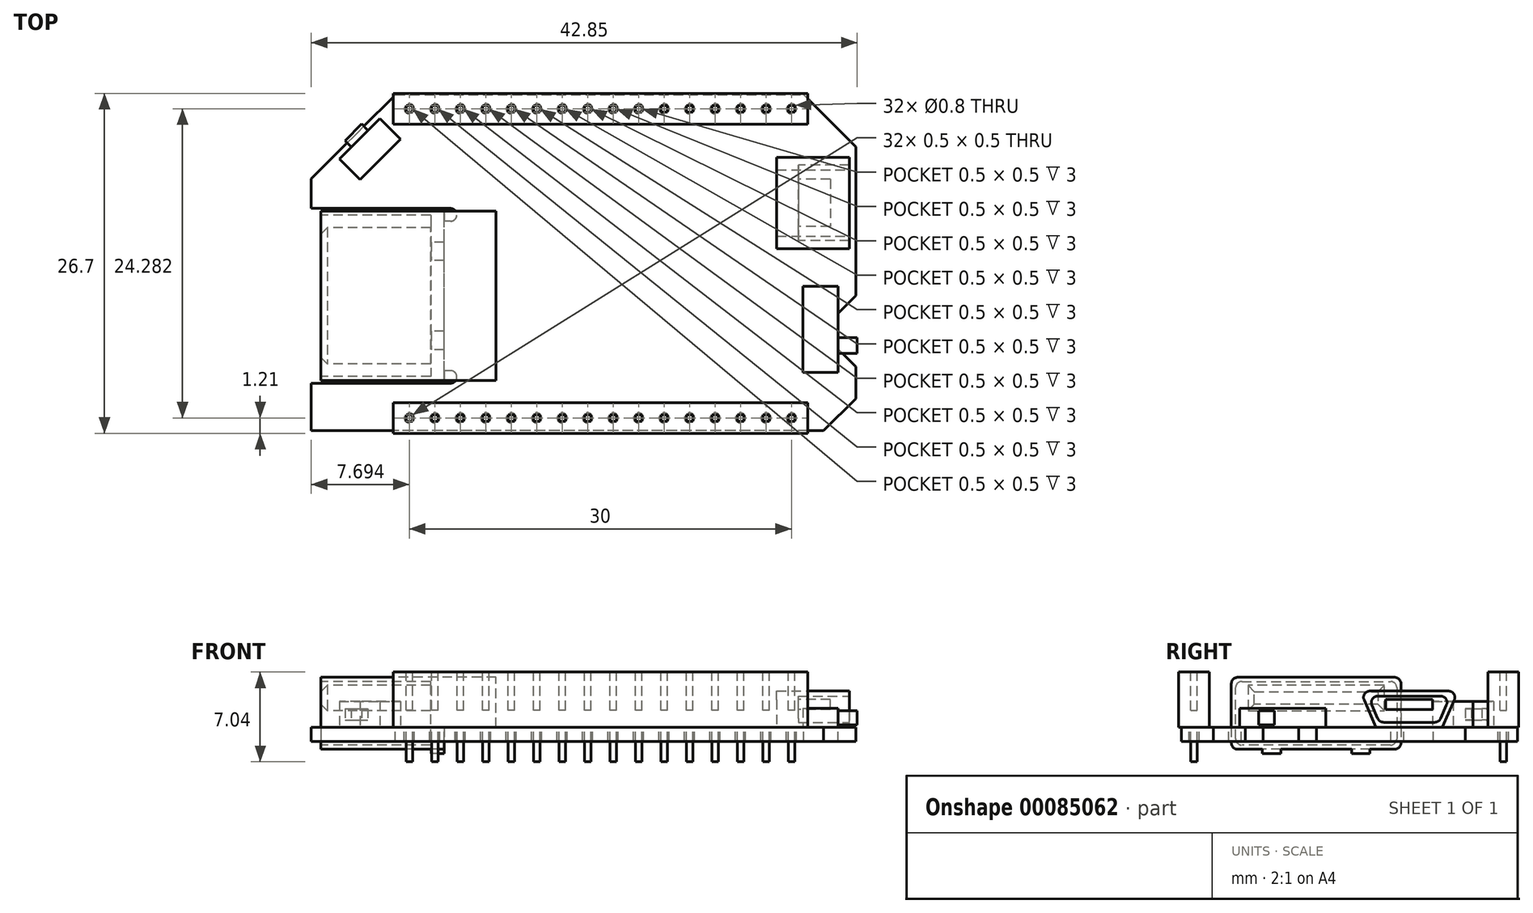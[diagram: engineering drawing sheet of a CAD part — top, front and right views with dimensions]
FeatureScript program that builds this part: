
annotation { "Feature Type Name" : "Feature", "Feature Type Description" : "" }
export const myFeature = defineFeature(function(context is Context, id is Id, definition is map)
    precondition{}
    {
        {
            var Q0;
            Q0=qCreatedBy(makeId("Top.planeOp"),FACE);
            var sketch = newSketch(context, id + "F0", { "sketchPlane" : qUnion([Q0])});
            skLineSegment(sketch, "E0", {"start": v(0, 19.78) * mm, "end": v(6.6, 26.37) * mm});
            skLineSegment(sketch, "E1", {"start": v(6.6, 26.37) * mm, "end": v(38.67, 26.37) * mm});
            skLineSegment(sketch, "E2", {"start": v(38.67, 26.37) * mm, "end": v(42.74, 22.3) * mm});
            skLineSegment(sketch, "E3", {"start": v(42.74, 22.3) * mm, "end": v(42.74, 10.6) * mm});
            skLineSegment(sketch, "E4", {"start": v(42.74, 2.52) * mm, "end": v(40.22, 0) * mm});
            skPoint(sketch, "E5.end.orphan", {"position": v(0, 0) * mm});
            skLineSegment(sketch, "E6", {"start": v(40.22, 0) * mm, "end": v(0, 0) * mm});
            skLineSegment(sketch, "E7", {"start": v(0, 3.71) * mm, "end": v(10.43, 3.71) * mm});
            skLineSegment(sketch, "E8", {"start": v(10.43, 3.71) * mm, "end": v(10.43, 17.45) * mm});
            skLineSegment(sketch, "E9", {"start": v(10.43, 17.45) * mm, "end": v(0, 17.45) * mm});
            skLineSegment(sketch, "E10", {"start": v(0, 17.45) * mm, "end": v(0, 19.78) * mm});
            skLineSegment(sketch, "E11", {"start": v(0, 3.71) * mm, "end": v(0, 0) * mm});
            skLineSegment(sketch, "E12", {"start": v(42.74, 10.6) * mm, "end": v(41.35, 9.2) * mm});
            skLineSegment(sketch, "E13", {"start": v(41.35, 9.2) * mm, "end": v(41.35, 6.41) * mm});
            skLineSegment(sketch, "E14", {"start": v(41.35, 6.41) * mm, "end": v(42.74, 5.02) * mm});
            skLineSegment(sketch, "E15.trimOffspring", {"start": v(42.74, 5.02) * mm, "end": v(42.74, 2.52) * mm});
            skSolve(sketch);
        }
        {
            var Q0;
            Q0 = qSketchRegion(id + "F0", true);
            extrude(context, id + "F1", {"entities" : qUnion([Q0]), "oppositeDirection" : true, "depth" : 1.1 * mm});
        }
        {
            var Q0;
            Q0=makeQuery(id+"F1.opExtrude","CAP_FACE",FACE,{"disambiguationData":[OSD([sQuery(id+"F0.wireOp",EDGE,"E0"),sQuery(id+"F0.wireOp",EDGE,"E1"),sQuery(id+"F0.wireOp",EDGE,"E2"),sQuery(id+"F0.wireOp",EDGE,"E3"),sQuery(id+"F0.wireOp",EDGE,"E4"),sQuery(id+"F0.wireOp",EDGE,"E6"),sQuery(id+"F0.wireOp",EDGE,"E7"),sQuery(id+"F0.wireOp",EDGE,"E8"),sQuery(id+"F0.wireOp",EDGE,"E9"),sQuery(id+"F0.wireOp",EDGE,"E10"),sQuery(id+"F0.wireOp",EDGE,"E11")])],"isStart":true});
            var sketch = newSketch(context, id + "F2", { "sketchPlane" : qUnion([Q0])});
            skArc(sketch, "E16", {"start": v(10.93, 16.45) * mm, "mid": v(11.43, 16.95) * mm, "end": v(10.93, 17.45) * mm});
            skArc(sketch, "E17", {"start": v(10.93, 3.71) * mm, "mid": v(11.43, 4.21) * mm, "end": v(10.93, 4.71) * mm});
            skLineSegment(sketch, "E18", {"start": v(10.43, 17.45) * mm, "end": v(10.93, 17.45) * mm});
            skLineSegment(sketch, "E19", {"start": v(10.93, 16.45) * mm, "end": v(10.43, 16.45) * mm});
            skLineSegment(sketch, "E20", {"start": v(10.43, 17.45) * mm, "end": v(10.43, 16.45) * mm});
            skPoint(sketch, "E21", {"position": v(11.43, 16.95) * mm});
            skLineSegment(sketch, "E22", {"start": v(10.43, 3.71) * mm, "end": v(10.93, 3.71) * mm});
            skLineSegment(sketch, "E23", {"start": v(10.43, 3.71) * mm, "end": v(10.43, 4.71) * mm});
            skLineSegment(sketch, "E24", {"start": v(10.43, 4.71) * mm, "end": v(10.93, 4.71) * mm});
            skSolve(sketch);
        }
        {
            var Q0;
            Q0 = qSketchRegion(id + "F2", true);
            extrude(context, id + "F3", {"entities" : qUnion([Q0]), "operationType" : NewBodyOperationType.REMOVE, "endBound" : BoundingType.THROUGH_ALL, "oppositeDirection" : true, "depth" : 25 * mm});
        }
        {
            var Q0;
            Q0=makeQuery(id+"F1.opExtrude","CAP_FACE",FACE,{"disambiguationData":[OSD([sQuery(id+"F0.wireOp",EDGE,"E0"),sQuery(id+"F0.wireOp",EDGE,"E1"),sQuery(id+"F0.wireOp",EDGE,"E2"),sQuery(id+"F0.wireOp",EDGE,"E3"),sQuery(id+"F0.wireOp",EDGE,"E4"),sQuery(id+"F0.wireOp",EDGE,"E6"),sQuery(id+"F0.wireOp",EDGE,"E7"),sQuery(id+"F0.wireOp",EDGE,"E8"),sQuery(id+"F0.wireOp",EDGE,"E9"),sQuery(id+"F0.wireOp",EDGE,"E10"),sQuery(id+"F0.wireOp",EDGE,"E11")])],"isStart":true});
            var sketch = newSketch(context, id + "F4", { "sketchPlane" : qUnion([Q0])});
            skCircle(sketch, "E25", {"center": v(7.7, 1) * mm, "radius": 0.4 * mm});
            skCircle(sketch, "E26", {"center": v(7.7, 25.27) * mm, "radius": 0.4 * mm});
            skCircle(sketch, "E27.1.0.0", {"center": v(9.7, 0.99) * mm, "radius": 0.4 * mm});
            skCircle(sketch, "E27.1.0.1", {"center": v(9.7, 25.27) * mm, "radius": 0.4 * mm});
            skCircle(sketch, "E27.2.0.0", {"center": v(11.7, 0.99) * mm, "radius": 0.4 * mm});
            skCircle(sketch, "E27.2.0.1", {"center": v(11.7, 25.27) * mm, "radius": 0.4 * mm});
            skLineSegment(sketch, "E27.direction1", {"start": v(7.7, 1) * mm, "end": v(9.7, 1) * mm, "construction": true});
            skCircle(sketch, "E28.0.3.0", {"center": v(13.7, 0.99) * mm, "radius": 0.4 * mm});
            skCircle(sketch, "E28.2.3.0", {"center": v(13.7, 25.27) * mm, "radius": 0.4 * mm});
            skCircle(sketch, "E28.0.4.0", {"center": v(15.7, 0.99) * mm, "radius": 0.4 * mm});
            skCircle(sketch, "E28.2.4.0", {"center": v(15.7, 25.27) * mm, "radius": 0.4 * mm});
            skCircle(sketch, "E28.0.5.0", {"center": v(17.7, 0.99) * mm, "radius": 0.4 * mm});
            skCircle(sketch, "E28.2.5.0", {"center": v(17.7, 25.27) * mm, "radius": 0.4 * mm});
            skCircle(sketch, "E28.0.6.0", {"center": v(19.7, 0.99) * mm, "radius": 0.4 * mm});
            skCircle(sketch, "E28.2.6.0", {"center": v(19.7, 25.27) * mm, "radius": 0.4 * mm});
            skCircle(sketch, "E28.0.7.0", {"center": v(21.7, 0.99) * mm, "radius": 0.4 * mm});
            skCircle(sketch, "E28.2.7.0", {"center": v(21.7, 25.27) * mm, "radius": 0.4 * mm});
            skCircle(sketch, "E28.0.8.0", {"center": v(23.7, 0.99) * mm, "radius": 0.4 * mm});
            skCircle(sketch, "E28.2.8.0", {"center": v(23.7, 25.27) * mm, "radius": 0.4 * mm});
            skCircle(sketch, "E28.0.9.0", {"center": v(25.7, 0.99) * mm, "radius": 0.4 * mm});
            skCircle(sketch, "E28.2.9.0", {"center": v(25.7, 25.27) * mm, "radius": 0.4 * mm});
            skCircle(sketch, "E28.0.10.0", {"center": v(27.7, 0.99) * mm, "radius": 0.4 * mm});
            skCircle(sketch, "E28.2.10.0", {"center": v(27.7, 25.27) * mm, "radius": 0.4 * mm});
            skCircle(sketch, "E28.0.11.0", {"center": v(29.7, 0.99) * mm, "radius": 0.4 * mm});
            skCircle(sketch, "E28.2.11.0", {"center": v(29.7, 25.27) * mm, "radius": 0.4 * mm});
            skCircle(sketch, "E28.0.12.0", {"center": v(31.7, 0.99) * mm, "radius": 0.4 * mm});
            skCircle(sketch, "E28.2.12.0", {"center": v(31.7, 25.27) * mm, "radius": 0.4 * mm});
            skCircle(sketch, "E28.0.13.0", {"center": v(33.7, 0.99) * mm, "radius": 0.4 * mm});
            skCircle(sketch, "E28.2.13.0", {"center": v(33.7, 25.27) * mm, "radius": 0.4 * mm});
            skCircle(sketch, "E28.0.14.0", {"center": v(35.7, 0.99) * mm, "radius": 0.4 * mm});
            skCircle(sketch, "E28.2.14.0", {"center": v(35.7, 25.27) * mm, "radius": 0.4 * mm});
            skCircle(sketch, "E28.0.15.0", {"center": v(37.7, 0.99) * mm, "radius": 0.4 * mm});
            skCircle(sketch, "E28.2.15.0", {"center": v(37.7, 25.27) * mm, "radius": 0.4 * mm});
            skSolve(sketch);
        }
        {
            var Q0;
            Q0 = qSketchRegion(id + "F4", true);
            extrude(context, id + "F5", {"entities" : qUnion([Q0]), "operationType" : NewBodyOperationType.REMOVE, "endBound" : BoundingType.THROUGH_ALL, "oppositeDirection" : true, "depth" : 25 * mm});
        }
        {
            var Q0;
            Q0=makeQuery(id+"F1.opExtrude","CAP_FACE",FACE,{"disambiguationData":[OSD([sQuery(id+"F0.wireOp",EDGE,"E0"),sQuery(id+"F0.wireOp",EDGE,"E1"),sQuery(id+"F0.wireOp",EDGE,"E2"),sQuery(id+"F0.wireOp",EDGE,"E3"),sQuery(id+"F0.wireOp",EDGE,"E4"),sQuery(id+"F0.wireOp",EDGE,"E6"),sQuery(id+"F0.wireOp",EDGE,"E7"),sQuery(id+"F0.wireOp",EDGE,"E8"),sQuery(id+"F0.wireOp",EDGE,"E9"),sQuery(id+"F0.wireOp",EDGE,"E10"),sQuery(id+"F0.wireOp",EDGE,"E11")])],"isStart":true});
            var sketch = newSketch(context, id + "F6", { "sketchPlane" : qUnion([Q0])});
            skLineSegment(sketch, "E29.bottom", {"start": v(6.42, 2.2) * mm, "end": v(38.97, 2.2) * mm});
            skLineSegment(sketch, "E29.top", {"start": v(6.42, -0.22) * mm, "end": v(38.97, -0.22) * mm});
            skLineSegment(sketch, "E29.left", {"start": v(6.42, 2.2) * mm, "end": v(6.42, -0.22) * mm});
            skLineSegment(sketch, "E29.right", {"start": v(38.97, 2.2) * mm, "end": v(38.97, -0.22) * mm});
            skCircle(sketch, "E30.0", {"center": v(7.7, 1) * mm, "radius": 0.4 * mm, "construction": true});
            skCircle(sketch, "E31.0", {"center": v(7.7, 25.27) * mm, "radius": 0.4 * mm, "construction": true});
            skLineSegment(sketch, "E32", {"start": v(6.42, 1) * mm, "end": v(38.97, 1) * mm, "construction": true});
            skLineSegment(sketch, "E33", {"start": v(22.7, 2.2) * mm, "end": v(22.7, -0.22) * mm, "construction": true});
            skCircle(sketch, "E34.0", {"center": v(21.7, 0.99) * mm, "radius": 0.4 * mm, "construction": true});
            skCircle(sketch, "E35.0", {"center": v(23.7, 0.99) * mm, "radius": 0.4 * mm, "construction": true});
            skLineSegment(sketch, "E36.bottom", {"start": v(6.42, 26.48) * mm, "end": v(38.97, 26.48) * mm});
            skLineSegment(sketch, "E36.top", {"start": v(6.42, 24.06) * mm, "end": v(38.97, 24.06) * mm});
            skLineSegment(sketch, "E36.left", {"start": v(6.42, 26.48) * mm, "end": v(6.42, 24.06) * mm});
            skLineSegment(sketch, "E36.right", {"start": v(38.97, 26.48) * mm, "end": v(38.97, 24.06) * mm});
            skLineSegment(sketch, "E37", {"start": v(6.42, 25.27) * mm, "end": v(38.97, 25.27) * mm, "construction": true});
            skSolve(sketch);
        }
        {
            var Q0;
            Q0 = qSketchRegion(id + "F6", true);
            extrude(context, id + "F7", {"entities" : qUnion([Q0]), "depth" : 4.34 * mm});
        }
        {
            var Q0;
            Q0=makeQuery(id+"F1.opExtrude","CAP_FACE",FACE,{"disambiguationData":[OSD([sQuery(id+"F0.wireOp",EDGE,"E0"),sQuery(id+"F0.wireOp",EDGE,"E1"),sQuery(id+"F0.wireOp",EDGE,"E2"),sQuery(id+"F0.wireOp",EDGE,"E3"),sQuery(id+"F0.wireOp",EDGE,"E4"),sQuery(id+"F0.wireOp",EDGE,"E6"),sQuery(id+"F0.wireOp",EDGE,"E7"),sQuery(id+"F0.wireOp",EDGE,"E8"),sQuery(id+"F0.wireOp",EDGE,"E9"),sQuery(id+"F0.wireOp",EDGE,"E10"),sQuery(id+"F0.wireOp",EDGE,"E11")])],"isStart":true});
            var sketch = newSketch(context, id + "F8", { "sketchPlane" : qUnion([Q0])});
            skLineSegment(sketch, "E38", {"start": v(2.2, 21.34) * mm, "end": v(5.38, 24.52) * mm});
            skLineSegment(sketch, "E39", {"start": v(5.38, 24.52) * mm, "end": v(7, 22.9) * mm});
            skLineSegment(sketch, "E40", {"start": v(7, 22.9) * mm, "end": v(3.83, 19.72) * mm});
            skLineSegment(sketch, "E41", {"start": v(3.83, 19.72) * mm, "end": v(2.2, 21.34) * mm});
            skSolve(sketch);
        }
        {
            var Q0;
            Q0=makeQuery(id+"F8.imprint","IMPRINT",FACE,{"disambiguationData":[TD([[makeQuery(id+"F8.imprint","IMPRINT",EDGE,{"derivedFrom":sQuery(id+"F8.wireOp",EDGE,"E38")}),-1.0]])]});
            extrude(context, id + "F9", {"entities" : qUnion([Q0]), "depth" : 2.05 * mm});
        }
        {
            var Q0;
            Q0=makeQuery(id+"F1.opExtrude","CAP_FACE",FACE,{"disambiguationData":[OSD([sQuery(id+"F0.wireOp",EDGE,"E0"),sQuery(id+"F0.wireOp",EDGE,"E1"),sQuery(id+"F0.wireOp",EDGE,"E2"),sQuery(id+"F0.wireOp",EDGE,"E3"),sQuery(id+"F0.wireOp",EDGE,"E4"),sQuery(id+"F0.wireOp",EDGE,"E6"),sQuery(id+"F0.wireOp",EDGE,"E7"),sQuery(id+"F0.wireOp",EDGE,"E8"),sQuery(id+"F0.wireOp",EDGE,"E9"),sQuery(id+"F0.wireOp",EDGE,"E10"),sQuery(id+"F0.wireOp",EDGE,"E11")])],"isStart":true});
            var sketch = newSketch(context, id + "F10", { "sketchPlane" : qUnion([Q0])});
            skLineSegment(sketch, "E42", {"start": v(39.67, 20.78) * mm, "end": v(39.67, 14.98) * mm, "construction": true});
            skLineSegment(sketch, "E43", {"start": v(39.67, 17.88) * mm, "end": v(42.24, 17.88) * mm, "construction": true});
            skLineSegment(sketch, "E44", {"start": v(39.67, 17.88) * mm, "end": v(36.54, 17.88) * mm, "construction": true});
            skSolve(sketch);
        }
        {
            var Q0;
            Q0=makeQuery(id+"F10.imprint","IMPRINT",FACE,{"disambiguationData":[TD([[makeQuery(id+"F10.imprint","IMPRINT",EDGE,{"derivedFrom":makeQuery(id+"F1.opExtrude","CAP_EDGE",EDGE,{"disambiguationData":[OSD([sQuery(id+"F0.wireOp",EDGE,"E0")])],"isStart":true})}),-1.0]])]});
            var sketch = newSketch(context, id + "F11", { "sketchPlane" : qUnion([Q0])});
            skLineSegment(sketch, "E45", {"start": v(40.05, 9.44) * mm, "end": v(40.05, 6.44) * mm, "construction": true});
            skLineSegment(sketch, "E46", {"start": v(38.6, 7.94) * mm, "end": v(41.35, 7.94) * mm, "construction": true});
            skPoint(sketch, "E47", {"position": v(40.05, 7.94) * mm});
            skLineSegment(sketch, "E48.bottom", {"start": v(38.6, 11.33) * mm, "end": v(41.35, 11.33) * mm});
            skLineSegment(sketch, "E48.top", {"start": v(38.6, 4.56) * mm, "end": v(41.35, 4.56) * mm});
            skLineSegment(sketch, "E48.left", {"start": v(38.6, 11.33) * mm, "end": v(38.6, 4.56) * mm});
            skLineSegment(sketch, "E48.right", {"start": v(41.35, 11.33) * mm, "end": v(41.35, 4.56) * mm});
            skSolve(sketch);
        }
        {
            var Q0;
            Q0=makeQuery(id+"F1.opExtrude","SWEPT_FACE",FACE,{"disambiguationData":[OSD([sQuery(id+"F0.wireOp",EDGE,"E11")])]});
            cPlane(context, id + "F12", {"entities" : qUnion([Q0]), "cplaneType" : CPlaneType.OFFSET, "offset" : .75 * mm, "oppositeDirection" : true, "width" : 150 * mm, "height" : 150 * mm});
        }
        {
            var Q0;
            Q0=qCreatedBy(id+"F12.planeOp",FACE);
            cPlane(context, id + "F13", {"entities" : qUnion([Q0]), "cplaneType" : CPlaneType.OFFSET, "offset" : 13.75 * mm, "oppositeDirection" : true, "width" : 150 * mm, "height" : 150 * mm});
        }
        {
            var Q0;
            Q0=qCreatedBy(id+"F12.planeOp",FACE);
            var sketch = newSketch(context, id + "F14", { "sketchPlane" : qUnion([Q0])});
            skLineSegment(sketch, "E49.0", {"start": v(-4.71, -1.1) * mm, "end": v(-16.45, -1.1) * mm, "construction": true});
            skLineSegment(sketch, "E50", {"start": v(-10.58, -1.1) * mm, "end": v(-10.58, 0.55) * mm, "construction": true});
            skLineSegment(sketch, "E51.bottom", {"start": v(-3.92, 3.93) * mm, "end": v(-17.24, 3.93) * mm});
            skLineSegment(sketch, "E51.top", {"start": v(-3.92, -1.72) * mm, "end": v(-17.24, -1.72) * mm});
            skLineSegment(sketch, "E51.left", {"start": v(-3.92, 3.93) * mm, "end": v(-3.92, -1.72) * mm});
            skLineSegment(sketch, "E51.right", {"start": v(-17.24, 3.93) * mm, "end": v(-17.24, -1.72) * mm});
            skPoint(sketch, "E51.middle", {"position": v(-10.58, 1.1) * mm});
            skSolve(sketch);
        }
        {
            var Q0;
            Q0 = qSketchRegion(id + "F14", true);
            var Q1;
            Q1=makeQuery(id+"F1.opExtrude","SWEPT_FACE",FACE,{"disambiguationData":[OSD([sQuery(id+"F0.wireOp",EDGE,"E8")])]});
            extrude(context, id + "F15", {"entities" : qUnion([Q0]), "endBound" : BoundingType.UP_TO_SURFACE, "oppositeDirection" : true, "endBoundEntityFace" : qUnion([Q1]), "depth" : 25 * mm});
        }
        {
            var Q0;
            Q0=makeQuery(id+"F15.opExtrude","CAP_FACE",FACE,{"disambiguationData":[OSD([sQuery(id+"F14.wireOp",EDGE,"E51.bottom"),sQuery(id+"F14.wireOp",EDGE,"E51.top"),sQuery(id+"F14.wireOp",EDGE,"E51.left"),sQuery(id+"F14.wireOp",EDGE,"E51.right")])],"isStart":false});
            var sketch = newSketch(context, id + "F16", { "sketchPlane" : qUnion([Q0])});
            skLineSegment(sketch, "E52.bottom", {"start": v(17.24, 3.93) * mm, "end": v(3.92, 3.93) * mm});
            skLineSegment(sketch, "E52.top", {"start": v(17.24, 0) * mm, "end": v(3.92, 0) * mm});
            skLineSegment(sketch, "E52.left", {"start": v(17.24, 3.93) * mm, "end": v(17.24, 0) * mm});
            skLineSegment(sketch, "E52.right", {"start": v(3.92, 3.93) * mm, "end": v(3.92, 0) * mm});
            skSolve(sketch);
        }
        {
            var Q0;
            Q0 = qSketchRegion(id + "F16", true);
            var Q1;
            Q1=qCreatedBy(id+"F13.planeOp",FACE);
            extrude(context, id + "F17", {"entities" : qUnion([Q0]), "operationType" : NewBodyOperationType.ADD, "endBound" : BoundingType.UP_TO_SURFACE, "endBoundEntityFace" : qUnion([Q1]), "depth" : 25 * mm});
        }
        {
            var Q0;
            Q0=makeQuery(id+"F15.opExtrude","CAP_FACE",FACE,{"disambiguationData":[OSD([sQuery(id+"F14.wireOp",EDGE,"E51.bottom"),sQuery(id+"F14.wireOp",EDGE,"E51.top"),sQuery(id+"F14.wireOp",EDGE,"E51.left"),sQuery(id+"F14.wireOp",EDGE,"E51.right")])],"isStart":true});
            var sketch = newSketch(context, id + "F18", { "sketchPlane" : qUnion([Q0])});
            skLineSegment(sketch, "E53.0", {"start": v(-4.25, -1.39) * mm, "end": v(-4.25, 3.6) * mm});
            skLineSegment(sketch, "E53.1", {"start": v(-16.91, -1.39) * mm, "end": v(-4.25, -1.39) * mm});
            skLineSegment(sketch, "E53.2", {"start": v(-16.91, 3.6) * mm, "end": v(-16.91, -1.39) * mm});
            skLineSegment(sketch, "E53.3", {"start": v(-4.25, 3.6) * mm, "end": v(-16.91, 3.6) * mm});
            skLineSegment(sketch, "E54.bottom", {"start": v(-5.23, 3.31) * mm, "end": v(-15.93, 3.31) * mm});
            skLineSegment(sketch, "E54.top", {"start": v(-5.23, 1.31) * mm, "end": v(-15.93, 1.31) * mm});
            skLineSegment(sketch, "E54.left", {"start": v(-5.23, 3.31) * mm, "end": v(-5.23, 1.31) * mm});
            skLineSegment(sketch, "E54.right", {"start": v(-15.93, 3.31) * mm, "end": v(-15.93, 1.31) * mm});
            skPoint(sketch, "E54.middle", {"position": v(-10.58, 2.31) * mm});
            skLineSegment(sketch, "E55", {"start": v(-10.58, 3.6) * mm, "end": v(-10.58, -1.39) * mm, "construction": true});
            skSolve(sketch);
        }
        {
            var Q0;
            Q0 = qSketchRegion(id + "F18", true);
            extrude(context, id + "F19", {"entities" : qUnion([Q0]), "operationType" : NewBodyOperationType.REMOVE, "oppositeDirection" : true, "depth" : 8.62 * mm});
        }
        {
            var Q0;
            Q0=makeQuery(id+"F19.boolean.opBoolean","COPY",EDGE,{"derivedFrom":makeQuery(id+"F19.opExtrude","CAP_EDGE",EDGE,{"disambiguationData":[OSD([sQuery(id+"F18.wireOp",EDGE,"E54.right")])],"isStart":true})});
            var Q1;
            Q1=makeQuery(id+"F19.boolean.opBoolean","COPY",EDGE,{"derivedFrom":makeQuery(id+"F19.opExtrude","CAP_EDGE",EDGE,{"disambiguationData":[OSD([sQuery(id+"F18.wireOp",EDGE,"E54.bottom")])],"isStart":true})});
            var Q2;
            Q2=makeQuery(id+"F19.boolean.opBoolean","COPY",EDGE,{"derivedFrom":makeQuery(id+"F19.opExtrude","CAP_EDGE",EDGE,{"disambiguationData":[OSD([sQuery(id+"F18.wireOp",EDGE,"E54.top")])],"isStart":true})});
            var Q3;
            Q3=makeQuery(id+"F19.boolean.opBoolean","COPY",EDGE,{"derivedFrom":makeQuery(id+"F19.opExtrude","CAP_EDGE",EDGE,{"disambiguationData":[OSD([sQuery(id+"F18.wireOp",EDGE,"E54.left")])],"isStart":true})});
            chamfer(context, id + "F20", {"entities" : qUnion([Q0, Q1, Q2, Q3]), "width" : .5 * mm, "tangentPropagation" : true});
        }
        {
            var Q0;
            Q0=makeQuery(id+"F17.boolean.opBoolean","MERGE",EDGE,{"derivedFrom":[makeQuery(id+"F15.opExtrude","SWEPT_EDGE",EDGE,{"disambiguationData":[OSD([sQuery(id+"F14.wireOp",EDGE,"E51.bottom"),sQuery(id+"F14.wireOp",EDGE,"E51.right")])]}),makeQuery(id+"F17.opExtrude","SWEPT_EDGE",EDGE,{"disambiguationData":[OSD([sQuery(id+"F16.wireOp",EDGE,"E52.bottom"),sQuery(id+"F16.wireOp",EDGE,"E52.left")])]})]});
            var Q1;
            Q1=makeQuery(id+"F19.boolean.opBoolean","COPY",EDGE,{"derivedFrom":makeQuery(id+"F19.opExtrude","SWEPT_EDGE",EDGE,{"disambiguationData":[OSD([sQuery(id+"F18.wireOp",EDGE,"E53.2"),sQuery(id+"F18.wireOp",EDGE,"E53.3")])]})});
            var Q2;
            Q2=makeQuery(id+"F17.boolean.opBoolean","MERGE",EDGE,{"derivedFrom":[makeQuery(id+"F15.opExtrude","SWEPT_EDGE",EDGE,{"disambiguationData":[OSD([sQuery(id+"F14.wireOp",EDGE,"E51.bottom"),sQuery(id+"F14.wireOp",EDGE,"E51.left")])]}),makeQuery(id+"F17.opExtrude","SWEPT_EDGE",EDGE,{"disambiguationData":[OSD([sQuery(id+"F16.wireOp",EDGE,"E52.bottom"),sQuery(id+"F16.wireOp",EDGE,"E52.right")])]})]});
            var Q3;
            Q3=makeQuery(id+"F19.boolean.opBoolean","COPY",EDGE,{"derivedFrom":makeQuery(id+"F19.opExtrude","SWEPT_EDGE",EDGE,{"disambiguationData":[OSD([sQuery(id+"F18.wireOp",EDGE,"E53.0"),sQuery(id+"F18.wireOp",EDGE,"E53.3")])]})});
            var Q4;
            Q4=makeQuery(id+"F19.boolean.opBoolean","COPY",EDGE,{"derivedFrom":makeQuery(id+"F19.opExtrude","SWEPT_EDGE",EDGE,{"disambiguationData":[OSD([sQuery(id+"F18.wireOp",EDGE,"E53.0"),sQuery(id+"F18.wireOp",EDGE,"E53.1")])]})});
            var Q5;
            Q5=makeQuery(id+"F19.boolean.opBoolean","COPY",EDGE,{"derivedFrom":makeQuery(id+"F19.opExtrude","SWEPT_EDGE",EDGE,{"disambiguationData":[OSD([sQuery(id+"F18.wireOp",EDGE,"E53.1"),sQuery(id+"F18.wireOp",EDGE,"E53.2")])]})});
            var Q6;
            Q6=makeQuery(id+"F15.opExtrude","SWEPT_EDGE",EDGE,{"disambiguationData":[OSD([sQuery(id+"F14.wireOp",EDGE,"E51.top"),sQuery(id+"F14.wireOp",EDGE,"E51.right")])]});
            var Q7;
            Q7=makeQuery(id+"F15.opExtrude","SWEPT_EDGE",EDGE,{"disambiguationData":[OSD([sQuery(id+"F14.wireOp",EDGE,"E51.top"),sQuery(id+"F14.wireOp",EDGE,"E51.left")])]});
            fillet(context, id + "F21", {"entities" : qUnion([Q0, Q1, Q2, Q3, Q4, Q5, Q6, Q7]), "radius" : .5 * mm, "tangentPropagation" : true, "allowEdgeOverflow" : false});
        }
        {
            var Q0;
            Q0 = qSketchRegion(id + "F11", true);
            extrude(context, id + "F22", {"entities" : qUnion([Q0]), "depth" : 1.5 * mm});
        }
        {
            var Q0;
            Q0=makeQuery(id+"F1.opExtrude","SWEPT_FACE",FACE,{"disambiguationData":[OSD([sQuery(id+"F0.wireOp",EDGE,"E3")])]});
            var Q1;
            Q1=sQuery(id+"F10.wireOp",VERTEX,"E43.end");
            cPlane(context, id + "F23", {"entities" : qUnion([Q0, Q1]), "cplaneType" : CPlaneType.PLANE_POINT, "offset" : 150 * mm, "width" : 150 * mm, "height" : 150 * mm});
        }
        {
            var Q0;
            Q0=qCreatedBy(id+"F23.planeOp",FACE);
            var Q1;
            Q1=sQuery(id+"F10.wireOp",VERTEX,"E44.end");
            cPlane(context, id + "F24", {"entities" : qUnion([Q0, Q1]), "cplaneType" : CPlaneType.PLANE_POINT, "offset" : 150 * mm, "width" : 150 * mm, "height" : 150 * mm});
        }
        {
            var Q0;
            Q0=qCreatedBy(id+"F23.planeOp",FACE);
            var sketch = newSketch(context, id + "F25", { "sketchPlane" : qUnion([Q0])});
            skLineSegment(sketch, "E56", {"start": v(14.03, 2.85) * mm, "end": v(15.28, 0) * mm});
            skLineSegment(sketch, "E57", {"start": v(15.28, 0) * mm, "end": v(20.48, 0) * mm});
            skLineSegment(sketch, "E58", {"start": v(20.48, 0) * mm, "end": v(21.73, 2.85) * mm});
            skLineSegment(sketch, "E59", {"start": v(21.73, 2.85) * mm, "end": v(14.03, 2.85) * mm});
            skPoint(sketch, "E60.0", {"position": v(17.88, 0) * mm});
            skLineSegment(sketch, "E61", {"start": v(17.88, 0) * mm, "end": v(17.88, 2.85) * mm, "construction": true});
            skSolve(sketch);
        }
        {
            var Q0;
            Q0=makeQuery(id+"F25.imprint","IMPRINT",FACE,{"disambiguationData":[TD([[makeQuery(id+"F25.imprint","IMPRINT",EDGE,{"derivedFrom":sQuery(id+"F25.wireOp",EDGE,"E56")}),1.0]])]});
            var Q1;
            Q1=qCreatedBy(id+"F24.planeOp",FACE);
            extrude(context, id + "F26", {"entities" : qUnion([Q0]), "operationType" : NewBodyOperationType.ADD, "endBound" : BoundingType.UP_TO_SURFACE, "oppositeDirection" : true, "endBoundEntityFace" : qUnion([Q1]), "depth" : 25 * mm});
        }
        {
            var Q0;
            Q0=makeQuery(id+"F26.opExtrude","CAP_FACE",FACE,{"disambiguationData":[OSD([sQuery(id+"F25.wireOp",EDGE,"E56"),sQuery(id+"F25.wireOp",EDGE,"E57"),sQuery(id+"F25.wireOp",EDGE,"E58"),sQuery(id+"F25.wireOp",EDGE,"E59")])],"isStart":true});
            var sketch = newSketch(context, id + "F27", { "sketchPlane" : qUnion([Q0])});
            skLineSegment(sketch, "E62.0", {"start": v(21.12, 2.45) * mm, "end": v(14.65, 2.45) * mm});
            skLineSegment(sketch, "E62.1", {"start": v(20.22, 0.4) * mm, "end": v(21.12, 2.45) * mm});
            skLineSegment(sketch, "E62.2", {"start": v(15.55, 0.4) * mm, "end": v(20.22, 0.4) * mm});
            skLineSegment(sketch, "E62.3", {"start": v(14.65, 2.45) * mm, "end": v(15.55, 0.4) * mm});
            skSolve(sketch);
        }
        {
            var Q0;
            Q0 = qSketchRegion(id + "F27", true);
            extrude(context, id + "F28", {"entities" : qUnion([Q0]), "operationType" : NewBodyOperationType.REMOVE, "oppositeDirection" : true, "depth" : 4 * mm});
        }
        {
            var Q0;
            Q0=makeQuery(id+"F28.boolean.opBoolean","COPY",FACE,{"derivedFrom":makeQuery(id+"F28.opExtrude","CAP_FACE",FACE,{"disambiguationData":[OSD([sQuery(id+"F27.wireOp",EDGE,"E62.0"),sQuery(id+"F27.wireOp",EDGE,"E62.1"),sQuery(id+"F27.wireOp",EDGE,"E62.2"),sQuery(id+"F27.wireOp",EDGE,"E62.3")])],"isStart":false})});
            var sketch = newSketch(context, id + "F29", { "sketchPlane" : qUnion([Q0])});
            skLineSegment(sketch, "E63.bottom", {"start": v(19.73, 1.4) * mm, "end": v(16.03, 1.4) * mm});
            skLineSegment(sketch, "E63.top", {"start": v(19.73, 2.2) * mm, "end": v(16.03, 2.2) * mm});
            skLineSegment(sketch, "E63.left", {"start": v(19.73, 1.4) * mm, "end": v(19.73, 2.2) * mm});
            skLineSegment(sketch, "E63.right", {"start": v(16.03, 1.4) * mm, "end": v(16.03, 2.2) * mm});
            skPoint(sketch, "E63.middle", {"position": v(17.88, 1.8) * mm});
            skSolve(sketch);
        }
        {
            var Q0;
            Q0=makeQuery(id+"F29.imprint","IMPRINT",FACE,{"disambiguationData":[TD([[makeQuery(id+"F29.imprint","IMPRINT",EDGE,{"derivedFrom":sQuery(id+"F29.wireOp",EDGE,"E63.bottom")}),-1.0]])]});
            extrude(context, id + "F30", {"entities" : qUnion([Q0]), "operationType" : NewBodyOperationType.ADD, "depth" : 2.5 * mm});
        }
        {
            var Q0;
            Q0=makeQuery(id+"F26.opExtrude","SWEPT_EDGE",EDGE,{"disambiguationData":[OSD([sQuery(id+"F25.wireOp",EDGE,"E56"),sQuery(id+"F25.wireOp",EDGE,"E59")])]});
            var Q1;
            Q1=makeQuery(id+"F26.opExtrude","SWEPT_EDGE",EDGE,{"disambiguationData":[OSD([sQuery(id+"F25.wireOp",EDGE,"E58"),sQuery(id+"F25.wireOp",EDGE,"E59")])]});
            var Q2;
            Q2=makeQuery(id+"F28.boolean.opBoolean","COPY",EDGE,{"derivedFrom":makeQuery(id+"F28.opExtrude","SWEPT_EDGE",EDGE,{"disambiguationData":[OSD([sQuery(id+"F27.wireOp",EDGE,"E62.0"),sQuery(id+"F27.wireOp",EDGE,"E62.1")])]})});
            var Q3;
            Q3=makeQuery(id+"F28.boolean.opBoolean","COPY",EDGE,{"derivedFrom":makeQuery(id+"F28.opExtrude","SWEPT_EDGE",EDGE,{"disambiguationData":[OSD([sQuery(id+"F27.wireOp",EDGE,"E62.0"),sQuery(id+"F27.wireOp",EDGE,"E62.3")])]})});
            var Q4;
            Q4=makeQuery(id+"F28.boolean.opBoolean","COPY",EDGE,{"derivedFrom":makeQuery(id+"F28.opExtrude","SWEPT_EDGE",EDGE,{"disambiguationData":[OSD([sQuery(id+"F27.wireOp",EDGE,"E62.1"),sQuery(id+"F27.wireOp",EDGE,"E62.2")])]})});
            var Q5;
            Q5=makeQuery(id+"F28.boolean.opBoolean","COPY",EDGE,{"derivedFrom":makeQuery(id+"F28.opExtrude","SWEPT_EDGE",EDGE,{"disambiguationData":[OSD([sQuery(id+"F27.wireOp",EDGE,"E62.2"),sQuery(id+"F27.wireOp",EDGE,"E62.3")])]})});
            fillet(context, id + "F31", {"entities" : qUnion([Q0, Q1, Q2, Q3, Q4, Q5]), "radius" : .5 * mm, "allowEdgeOverflow" : false});
        }
        {
            var Q0;
            Q0=makeQuery(id+"F15.opExtrude","SWEPT_FACE",FACE,{"disambiguationData":[OSD([sQuery(id+"F14.wireOp",EDGE,"E51.top")])]});
            var sketch = newSketch(context, id + "F32", { "sketchPlane" : qUnion([Q0])});
            skLineSegment(sketch, "E64.bottom", {"start": v(10.43, -14.8) * mm, "end": v(9.43, -14.8) * mm});
            skLineSegment(sketch, "E64.top", {"start": v(10.43, -13.36) * mm, "end": v(9.43, -13.36) * mm});
            skLineSegment(sketch, "E64.left", {"start": v(10.43, -14.8) * mm, "end": v(10.43, -13.36) * mm});
            skLineSegment(sketch, "E64.right", {"start": v(9.43, -14.8) * mm, "end": v(9.43, -13.36) * mm});
            skLineSegment(sketch, "E65.bottom", {"start": v(10.43, -7.8) * mm, "end": v(9.43, -7.8) * mm});
            skLineSegment(sketch, "E65.top", {"start": v(10.43, -6.36) * mm, "end": v(9.43, -6.36) * mm});
            skLineSegment(sketch, "E65.left", {"start": v(10.43, -7.8) * mm, "end": v(10.43, -6.36) * mm});
            skLineSegment(sketch, "E65.right", {"start": v(9.43, -7.8) * mm, "end": v(9.43, -6.36) * mm});
            skLineSegment(sketch, "E66", {"start": v(10.43, -10.58) * mm, "end": v(0.75, -10.58) * mm, "construction": true});
            skSolve(sketch);
        }
        {
            var Q0;
            Q0 = qSketchRegion(id + "F32", true);
            extrude(context, id + "F33", {"entities" : qUnion([Q0]), "operationType" : NewBodyOperationType.ADD, "depth" : .35 * mm});
        }
        {
            var Q0;
            Q0=makeQuery(id+"F1.opExtrude","CAP_FACE",FACE,{"disambiguationData":[OSD([sQuery(id+"F0.wireOp",EDGE,"E0"),sQuery(id+"F0.wireOp",EDGE,"E1"),sQuery(id+"F0.wireOp",EDGE,"E2"),sQuery(id+"F0.wireOp",EDGE,"E3"),sQuery(id+"F0.wireOp",EDGE,"E4"),sQuery(id+"F0.wireOp",EDGE,"E6"),sQuery(id+"F0.wireOp",EDGE,"E7"),sQuery(id+"F0.wireOp",EDGE,"E8"),sQuery(id+"F0.wireOp",EDGE,"E9"),sQuery(id+"F0.wireOp",EDGE,"E10"),sQuery(id+"F0.wireOp",EDGE,"E11"),sQuery(id+"F0.wireOp",EDGE,"E12"),sQuery(id+"F0.wireOp",EDGE,"E13"),sQuery(id+"F0.wireOp",EDGE,"E14"),sQuery(id+"F0.wireOp",EDGE,"E15.trimOffspring")])],"isStart":false});
            cPlane(context, id + "F34", {"entities" : qUnion([Q0]), "cplaneType" : CPlaneType.OFFSET, "offset" : 1.6 * mm, "width" : 150 * mm, "height" : 150 * mm});
        }
        {
            var Q0;
            Q0=makeQuery(id+"F7.opExtrude","CAP_FACE",FACE,{"disambiguationData":[OSD([sQuery(id+"F6.wireOp",EDGE,"E29.bottom"),sQuery(id+"F6.wireOp",EDGE,"E29.top"),sQuery(id+"F6.wireOp",EDGE,"E29.left"),sQuery(id+"F6.wireOp",EDGE,"E29.right")])],"isStart":false});
            var sketch = newSketch(context, id + "F35", { "sketchPlane" : qUnion([Q0])});
            skCircle(sketch, "E67.0", {"center": v(7.7, 1) * mm, "radius": 0.4 * mm, "construction": true});
            skCircle(sketch, "E68.0", {"center": v(7.7, 25.27) * mm, "radius": 0.4 * mm, "construction": true});
            skLineSegment(sketch, "E69.bottom", {"start": v(7.94, 0.74) * mm, "end": v(7.44, 0.74) * mm});
            skLineSegment(sketch, "E69.top", {"start": v(7.94, 1.24) * mm, "end": v(7.44, 1.24) * mm});
            skLineSegment(sketch, "E69.left", {"start": v(7.94, 0.74) * mm, "end": v(7.94, 1.24) * mm});
            skLineSegment(sketch, "E69.right", {"start": v(7.44, 0.74) * mm, "end": v(7.44, 1.24) * mm});
            skLineSegment(sketch, "E70.bottom", {"start": v(7.94, 25.02) * mm, "end": v(7.44, 25.02) * mm});
            skLineSegment(sketch, "E70.top", {"start": v(7.94, 25.52) * mm, "end": v(7.44, 25.52) * mm});
            skLineSegment(sketch, "E70.left", {"start": v(7.94, 25.02) * mm, "end": v(7.94, 25.52) * mm});
            skLineSegment(sketch, "E70.right", {"start": v(7.44, 25.02) * mm, "end": v(7.44, 25.52) * mm});
            skLineSegment(sketch, "E71.1.0.0", {"start": v(9.94, 0.74) * mm, "end": v(9.94, 1.24) * mm});
            skLineSegment(sketch, "E71.1.0.1", {"start": v(9.94, 0.74) * mm, "end": v(9.44, 0.74) * mm});
            skLineSegment(sketch, "E71.1.0.2", {"start": v(9.94, 1.24) * mm, "end": v(9.44, 1.24) * mm});
            skLineSegment(sketch, "E71.1.0.3", {"start": v(9.44, 0.74) * mm, "end": v(9.44, 1.24) * mm});
            skLineSegment(sketch, "E71.1.0.4", {"start": v(9.94, 25.02) * mm, "end": v(9.94, 25.52) * mm});
            skLineSegment(sketch, "E71.1.0.5", {"start": v(9.94, 25.02) * mm, "end": v(9.44, 25.02) * mm});
            skLineSegment(sketch, "E71.1.0.6", {"start": v(9.44, 25.02) * mm, "end": v(9.44, 25.52) * mm});
            skLineSegment(sketch, "E71.1.0.7", {"start": v(9.94, 25.52) * mm, "end": v(9.44, 25.52) * mm});
            skLineSegment(sketch, "E71.2.0.0", {"start": v(11.94, 0.74) * mm, "end": v(11.94, 1.24) * mm});
            skLineSegment(sketch, "E71.2.0.1", {"start": v(11.94, 0.74) * mm, "end": v(11.44, 0.74) * mm});
            skLineSegment(sketch, "E71.2.0.2", {"start": v(11.94, 1.24) * mm, "end": v(11.44, 1.24) * mm});
            skLineSegment(sketch, "E71.2.0.3", {"start": v(11.44, 0.74) * mm, "end": v(11.44, 1.24) * mm});
            skLineSegment(sketch, "E71.2.0.4", {"start": v(11.94, 25.02) * mm, "end": v(11.94, 25.52) * mm});
            skLineSegment(sketch, "E71.2.0.5", {"start": v(11.94, 25.02) * mm, "end": v(11.44, 25.02) * mm});
            skLineSegment(sketch, "E71.2.0.6", {"start": v(11.44, 25.02) * mm, "end": v(11.44, 25.52) * mm});
            skLineSegment(sketch, "E71.2.0.7", {"start": v(11.94, 25.52) * mm, "end": v(11.44, 25.52) * mm});
            skLineSegment(sketch, "E71.3.0.0", {"start": v(13.94, 0.74) * mm, "end": v(13.94, 1.24) * mm});
            skLineSegment(sketch, "E71.3.0.1", {"start": v(13.94, 0.74) * mm, "end": v(13.44, 0.74) * mm});
            skLineSegment(sketch, "E71.3.0.2", {"start": v(13.94, 1.24) * mm, "end": v(13.44, 1.24) * mm});
            skLineSegment(sketch, "E71.3.0.3", {"start": v(13.44, 0.74) * mm, "end": v(13.44, 1.24) * mm});
            skLineSegment(sketch, "E71.3.0.4", {"start": v(13.94, 25.02) * mm, "end": v(13.94, 25.52) * mm});
            skLineSegment(sketch, "E71.3.0.5", {"start": v(13.94, 25.02) * mm, "end": v(13.44, 25.02) * mm});
            skLineSegment(sketch, "E71.3.0.6", {"start": v(13.44, 25.02) * mm, "end": v(13.44, 25.52) * mm});
            skLineSegment(sketch, "E71.3.0.7", {"start": v(13.94, 25.52) * mm, "end": v(13.44, 25.52) * mm});
            skLineSegment(sketch, "E71.4.0.0", {"start": v(15.94, 0.74) * mm, "end": v(15.94, 1.24) * mm});
            skLineSegment(sketch, "E71.4.0.1", {"start": v(15.94, 0.74) * mm, "end": v(15.44, 0.74) * mm});
            skLineSegment(sketch, "E71.4.0.2", {"start": v(15.94, 1.24) * mm, "end": v(15.44, 1.24) * mm});
            skLineSegment(sketch, "E71.4.0.3", {"start": v(15.44, 0.74) * mm, "end": v(15.44, 1.24) * mm});
            skLineSegment(sketch, "E71.4.0.4", {"start": v(15.94, 25.02) * mm, "end": v(15.94, 25.52) * mm});
            skLineSegment(sketch, "E71.4.0.5", {"start": v(15.94, 25.02) * mm, "end": v(15.44, 25.02) * mm});
            skLineSegment(sketch, "E71.4.0.6", {"start": v(15.44, 25.02) * mm, "end": v(15.44, 25.52) * mm});
            skLineSegment(sketch, "E71.4.0.7", {"start": v(15.94, 25.52) * mm, "end": v(15.44, 25.52) * mm});
            skLineSegment(sketch, "E71.5.0.0", {"start": v(17.94, 0.74) * mm, "end": v(17.94, 1.24) * mm});
            skLineSegment(sketch, "E71.5.0.1", {"start": v(17.94, 0.74) * mm, "end": v(17.44, 0.74) * mm});
            skLineSegment(sketch, "E71.5.0.2", {"start": v(17.94, 1.24) * mm, "end": v(17.44, 1.24) * mm});
            skLineSegment(sketch, "E71.5.0.3", {"start": v(17.44, 0.74) * mm, "end": v(17.44, 1.24) * mm});
            skLineSegment(sketch, "E71.5.0.4", {"start": v(17.94, 25.02) * mm, "end": v(17.94, 25.52) * mm});
            skLineSegment(sketch, "E71.5.0.5", {"start": v(17.94, 25.02) * mm, "end": v(17.44, 25.02) * mm});
            skLineSegment(sketch, "E71.5.0.6", {"start": v(17.44, 25.02) * mm, "end": v(17.44, 25.52) * mm});
            skLineSegment(sketch, "E71.5.0.7", {"start": v(17.94, 25.52) * mm, "end": v(17.44, 25.52) * mm});
            skLineSegment(sketch, "E71.6.0.0", {"start": v(19.94, 0.74) * mm, "end": v(19.94, 1.24) * mm});
            skLineSegment(sketch, "E71.6.0.1", {"start": v(19.94, 0.74) * mm, "end": v(19.44, 0.74) * mm});
            skLineSegment(sketch, "E71.6.0.2", {"start": v(19.94, 1.24) * mm, "end": v(19.44, 1.24) * mm});
            skLineSegment(sketch, "E71.6.0.3", {"start": v(19.44, 0.74) * mm, "end": v(19.44, 1.24) * mm});
            skLineSegment(sketch, "E71.6.0.4", {"start": v(19.94, 25.02) * mm, "end": v(19.94, 25.52) * mm});
            skLineSegment(sketch, "E71.6.0.5", {"start": v(19.94, 25.02) * mm, "end": v(19.44, 25.02) * mm});
            skLineSegment(sketch, "E71.6.0.6", {"start": v(19.44, 25.02) * mm, "end": v(19.44, 25.52) * mm});
            skLineSegment(sketch, "E71.6.0.7", {"start": v(19.94, 25.52) * mm, "end": v(19.44, 25.52) * mm});
            skLineSegment(sketch, "E71.7.0.0", {"start": v(21.94, 0.74) * mm, "end": v(21.94, 1.24) * mm});
            skLineSegment(sketch, "E71.7.0.1", {"start": v(21.94, 0.74) * mm, "end": v(21.44, 0.74) * mm});
            skLineSegment(sketch, "E71.7.0.2", {"start": v(21.94, 1.24) * mm, "end": v(21.44, 1.24) * mm});
            skLineSegment(sketch, "E71.7.0.3", {"start": v(21.44, 0.74) * mm, "end": v(21.44, 1.24) * mm});
            skLineSegment(sketch, "E71.7.0.4", {"start": v(21.94, 25.02) * mm, "end": v(21.94, 25.52) * mm});
            skLineSegment(sketch, "E71.7.0.5", {"start": v(21.94, 25.02) * mm, "end": v(21.44, 25.02) * mm});
            skLineSegment(sketch, "E71.7.0.6", {"start": v(21.44, 25.02) * mm, "end": v(21.44, 25.52) * mm});
            skLineSegment(sketch, "E71.7.0.7", {"start": v(21.94, 25.52) * mm, "end": v(21.44, 25.52) * mm});
            skLineSegment(sketch, "E71.8.0.0", {"start": v(23.94, 0.74) * mm, "end": v(23.94, 1.24) * mm});
            skLineSegment(sketch, "E71.8.0.1", {"start": v(23.94, 0.74) * mm, "end": v(23.44, 0.74) * mm});
            skLineSegment(sketch, "E71.8.0.2", {"start": v(23.94, 1.24) * mm, "end": v(23.44, 1.24) * mm});
            skLineSegment(sketch, "E71.8.0.3", {"start": v(23.44, 0.74) * mm, "end": v(23.44, 1.24) * mm});
            skLineSegment(sketch, "E71.8.0.4", {"start": v(23.94, 25.02) * mm, "end": v(23.94, 25.52) * mm});
            skLineSegment(sketch, "E71.8.0.5", {"start": v(23.94, 25.02) * mm, "end": v(23.44, 25.02) * mm});
            skLineSegment(sketch, "E71.8.0.6", {"start": v(23.44, 25.02) * mm, "end": v(23.44, 25.52) * mm});
            skLineSegment(sketch, "E71.8.0.7", {"start": v(23.94, 25.52) * mm, "end": v(23.44, 25.52) * mm});
            skLineSegment(sketch, "E71.9.0.0", {"start": v(25.94, 0.74) * mm, "end": v(25.94, 1.24) * mm});
            skLineSegment(sketch, "E71.9.0.1", {"start": v(25.94, 0.74) * mm, "end": v(25.44, 0.74) * mm});
            skLineSegment(sketch, "E71.9.0.2", {"start": v(25.94, 1.24) * mm, "end": v(25.44, 1.24) * mm});
            skLineSegment(sketch, "E71.9.0.3", {"start": v(25.44, 0.74) * mm, "end": v(25.44, 1.24) * mm});
            skLineSegment(sketch, "E71.9.0.4", {"start": v(25.94, 25.02) * mm, "end": v(25.94, 25.52) * mm});
            skLineSegment(sketch, "E71.9.0.5", {"start": v(25.94, 25.02) * mm, "end": v(25.44, 25.02) * mm});
            skLineSegment(sketch, "E71.9.0.6", {"start": v(25.44, 25.02) * mm, "end": v(25.44, 25.52) * mm});
            skLineSegment(sketch, "E71.9.0.7", {"start": v(25.94, 25.52) * mm, "end": v(25.44, 25.52) * mm});
            skLineSegment(sketch, "E71.10.0.0", {"start": v(27.94, 0.74) * mm, "end": v(27.94, 1.24) * mm});
            skLineSegment(sketch, "E71.10.0.1", {"start": v(27.94, 0.74) * mm, "end": v(27.44, 0.74) * mm});
            skLineSegment(sketch, "E71.10.0.2", {"start": v(27.94, 1.24) * mm, "end": v(27.44, 1.24) * mm});
            skLineSegment(sketch, "E71.10.0.3", {"start": v(27.44, 0.74) * mm, "end": v(27.44, 1.24) * mm});
            skLineSegment(sketch, "E71.10.0.4", {"start": v(27.94, 25.02) * mm, "end": v(27.94, 25.52) * mm});
            skLineSegment(sketch, "E71.10.0.5", {"start": v(27.94, 25.02) * mm, "end": v(27.44, 25.02) * mm});
            skLineSegment(sketch, "E71.10.0.6", {"start": v(27.44, 25.02) * mm, "end": v(27.44, 25.52) * mm});
            skLineSegment(sketch, "E71.10.0.7", {"start": v(27.94, 25.52) * mm, "end": v(27.44, 25.52) * mm});
            skLineSegment(sketch, "E71.11.0.0", {"start": v(29.94, 0.74) * mm, "end": v(29.94, 1.24) * mm});
            skLineSegment(sketch, "E71.11.0.1", {"start": v(29.94, 0.74) * mm, "end": v(29.44, 0.74) * mm});
            skLineSegment(sketch, "E71.11.0.2", {"start": v(29.94, 1.24) * mm, "end": v(29.44, 1.24) * mm});
            skLineSegment(sketch, "E71.11.0.3", {"start": v(29.44, 0.74) * mm, "end": v(29.44, 1.24) * mm});
            skLineSegment(sketch, "E71.11.0.4", {"start": v(29.94, 25.02) * mm, "end": v(29.94, 25.52) * mm});
            skLineSegment(sketch, "E71.11.0.5", {"start": v(29.94, 25.02) * mm, "end": v(29.44, 25.02) * mm});
            skLineSegment(sketch, "E71.11.0.6", {"start": v(29.44, 25.02) * mm, "end": v(29.44, 25.52) * mm});
            skLineSegment(sketch, "E71.11.0.7", {"start": v(29.94, 25.52) * mm, "end": v(29.44, 25.52) * mm});
            skLineSegment(sketch, "E71.12.0.0", {"start": v(31.94, 0.74) * mm, "end": v(31.94, 1.24) * mm});
            skLineSegment(sketch, "E71.12.0.1", {"start": v(31.94, 0.74) * mm, "end": v(31.44, 0.74) * mm});
            skLineSegment(sketch, "E71.12.0.2", {"start": v(31.94, 1.24) * mm, "end": v(31.44, 1.24) * mm});
            skLineSegment(sketch, "E71.12.0.3", {"start": v(31.44, 0.74) * mm, "end": v(31.44, 1.24) * mm});
            skLineSegment(sketch, "E71.12.0.4", {"start": v(31.94, 25.02) * mm, "end": v(31.94, 25.52) * mm});
            skLineSegment(sketch, "E71.12.0.5", {"start": v(31.94, 25.02) * mm, "end": v(31.44, 25.02) * mm});
            skLineSegment(sketch, "E71.12.0.6", {"start": v(31.44, 25.02) * mm, "end": v(31.44, 25.52) * mm});
            skLineSegment(sketch, "E71.12.0.7", {"start": v(31.94, 25.52) * mm, "end": v(31.44, 25.52) * mm});
            skLineSegment(sketch, "E71.13.0.0", {"start": v(33.94, 0.74) * mm, "end": v(33.94, 1.24) * mm});
            skLineSegment(sketch, "E71.13.0.1", {"start": v(33.94, 0.74) * mm, "end": v(33.44, 0.74) * mm});
            skLineSegment(sketch, "E71.13.0.2", {"start": v(33.94, 1.24) * mm, "end": v(33.44, 1.24) * mm});
            skLineSegment(sketch, "E71.13.0.3", {"start": v(33.44, 0.74) * mm, "end": v(33.44, 1.24) * mm});
            skLineSegment(sketch, "E71.13.0.4", {"start": v(33.94, 25.02) * mm, "end": v(33.94, 25.52) * mm});
            skLineSegment(sketch, "E71.13.0.5", {"start": v(33.94, 25.02) * mm, "end": v(33.44, 25.02) * mm});
            skLineSegment(sketch, "E71.13.0.6", {"start": v(33.44, 25.02) * mm, "end": v(33.44, 25.52) * mm});
            skLineSegment(sketch, "E71.13.0.7", {"start": v(33.94, 25.52) * mm, "end": v(33.44, 25.52) * mm});
            skLineSegment(sketch, "E71.14.0.0", {"start": v(35.94, 0.74) * mm, "end": v(35.94, 1.24) * mm});
            skLineSegment(sketch, "E71.14.0.1", {"start": v(35.94, 0.74) * mm, "end": v(35.44, 0.74) * mm});
            skLineSegment(sketch, "E71.14.0.2", {"start": v(35.94, 1.24) * mm, "end": v(35.44, 1.24) * mm});
            skLineSegment(sketch, "E71.14.0.3", {"start": v(35.44, 0.74) * mm, "end": v(35.44, 1.24) * mm});
            skLineSegment(sketch, "E71.14.0.4", {"start": v(35.94, 25.02) * mm, "end": v(35.94, 25.52) * mm});
            skLineSegment(sketch, "E71.14.0.5", {"start": v(35.94, 25.02) * mm, "end": v(35.44, 25.02) * mm});
            skLineSegment(sketch, "E71.14.0.6", {"start": v(35.44, 25.02) * mm, "end": v(35.44, 25.52) * mm});
            skLineSegment(sketch, "E71.14.0.7", {"start": v(35.94, 25.52) * mm, "end": v(35.44, 25.52) * mm});
            skLineSegment(sketch, "E71.15.0.0", {"start": v(37.94, 0.74) * mm, "end": v(37.94, 1.24) * mm});
            skLineSegment(sketch, "E71.15.0.1", {"start": v(37.94, 0.74) * mm, "end": v(37.44, 0.74) * mm});
            skLineSegment(sketch, "E71.15.0.2", {"start": v(37.94, 1.24) * mm, "end": v(37.44, 1.24) * mm});
            skLineSegment(sketch, "E71.15.0.3", {"start": v(37.44, 0.74) * mm, "end": v(37.44, 1.24) * mm});
            skLineSegment(sketch, "E71.15.0.4", {"start": v(37.94, 25.02) * mm, "end": v(37.94, 25.52) * mm});
            skLineSegment(sketch, "E71.15.0.5", {"start": v(37.94, 25.02) * mm, "end": v(37.44, 25.02) * mm});
            skLineSegment(sketch, "E71.15.0.6", {"start": v(37.44, 25.02) * mm, "end": v(37.44, 25.52) * mm});
            skLineSegment(sketch, "E71.15.0.7", {"start": v(37.94, 25.52) * mm, "end": v(37.44, 25.52) * mm});
            skLineSegment(sketch, "E71.direction1", {"start": v(7.94, 0.74) * mm, "end": v(9.94, 0.74) * mm, "construction": true});
            skSolve(sketch);
        }
        {
            var Q0;
            Q0 = qSketchRegion(id + "F35", true);
            extrude(context, id + "F36", {"entities" : qUnion([Q0]), "operationType" : NewBodyOperationType.REMOVE, "oppositeDirection" : true, "depth" : 3 * mm});
        }
        {
            var Q0;
            Q0=makeQuery(id+"F7.opExtrude","CAP_FACE",FACE,{"disambiguationData":[OSD([sQuery(id+"F6.wireOp",EDGE,"E36.bottom"),sQuery(id+"F6.wireOp",EDGE,"E36.top"),sQuery(id+"F6.wireOp",EDGE,"E36.left"),sQuery(id+"F6.wireOp",EDGE,"E36.right")])],"isStart":true});
            var sketch = newSketch(context, id + "F37", { "sketchPlane" : qUnion([Q0])});
            skLineSegment(sketch, "E72.0.0", {"start": v(37.44, -25.02) * mm, "end": v(37.94, -25.02) * mm});
            skLineSegment(sketch, "E72.0.1", {"start": v(37.94, -25.02) * mm, "end": v(37.94, -25.52) * mm});
            skLineSegment(sketch, "E72.0.2", {"start": v(37.94, -25.52) * mm, "end": v(37.44, -25.52) * mm});
            skLineSegment(sketch, "E72.0.3", {"start": v(37.44, -25.52) * mm, "end": v(37.44, -25.02) * mm});
            skLineSegment(sketch, "E73.0.0", {"start": v(35.44, -25.02) * mm, "end": v(35.94, -25.02) * mm});
            skLineSegment(sketch, "E73.0.1", {"start": v(35.94, -25.02) * mm, "end": v(35.94, -25.52) * mm});
            skLineSegment(sketch, "E73.0.2", {"start": v(35.94, -25.52) * mm, "end": v(35.44, -25.52) * mm});
            skLineSegment(sketch, "E73.0.3", {"start": v(35.44, -25.52) * mm, "end": v(35.44, -25.02) * mm});
            skLineSegment(sketch, "E74.0.0", {"start": v(33.44, -25.02) * mm, "end": v(33.94, -25.02) * mm});
            skLineSegment(sketch, "E74.0.1", {"start": v(33.94, -25.02) * mm, "end": v(33.94, -25.52) * mm});
            skLineSegment(sketch, "E74.0.2", {"start": v(33.94, -25.52) * mm, "end": v(33.44, -25.52) * mm});
            skLineSegment(sketch, "E74.0.3", {"start": v(33.44, -25.52) * mm, "end": v(33.44, -25.02) * mm});
            skLineSegment(sketch, "E75.0.0", {"start": v(31.44, -25.02) * mm, "end": v(31.94, -25.02) * mm});
            skLineSegment(sketch, "E75.0.1", {"start": v(31.94, -25.02) * mm, "end": v(31.94, -25.52) * mm});
            skLineSegment(sketch, "E75.0.2", {"start": v(31.94, -25.52) * mm, "end": v(31.44, -25.52) * mm});
            skLineSegment(sketch, "E75.0.3", {"start": v(31.44, -25.52) * mm, "end": v(31.44, -25.02) * mm});
            skLineSegment(sketch, "E76.0.0", {"start": v(29.44, -25.02) * mm, "end": v(29.94, -25.02) * mm});
            skLineSegment(sketch, "E76.0.1", {"start": v(29.94, -25.02) * mm, "end": v(29.94, -25.52) * mm});
            skLineSegment(sketch, "E76.0.2", {"start": v(29.94, -25.52) * mm, "end": v(29.44, -25.52) * mm});
            skLineSegment(sketch, "E76.0.3", {"start": v(29.44, -25.52) * mm, "end": v(29.44, -25.02) * mm});
            skLineSegment(sketch, "E77.0.0", {"start": v(27.44, -25.02) * mm, "end": v(27.94, -25.02) * mm});
            skLineSegment(sketch, "E77.0.1", {"start": v(27.94, -25.02) * mm, "end": v(27.94, -25.52) * mm});
            skLineSegment(sketch, "E77.0.2", {"start": v(27.94, -25.52) * mm, "end": v(27.44, -25.52) * mm});
            skLineSegment(sketch, "E77.0.3", {"start": v(27.44, -25.52) * mm, "end": v(27.44, -25.02) * mm});
            skLineSegment(sketch, "E78.0.0", {"start": v(25.44, -25.02) * mm, "end": v(25.94, -25.02) * mm});
            skLineSegment(sketch, "E78.0.1", {"start": v(25.94, -25.02) * mm, "end": v(25.94, -25.52) * mm});
            skLineSegment(sketch, "E78.0.2", {"start": v(25.94, -25.52) * mm, "end": v(25.44, -25.52) * mm});
            skLineSegment(sketch, "E78.0.3", {"start": v(25.44, -25.52) * mm, "end": v(25.44, -25.02) * mm});
            skLineSegment(sketch, "E79.0.0", {"start": v(23.44, -25.02) * mm, "end": v(23.94, -25.02) * mm});
            skLineSegment(sketch, "E79.0.1", {"start": v(23.94, -25.02) * mm, "end": v(23.94, -25.52) * mm});
            skLineSegment(sketch, "E79.0.2", {"start": v(23.94, -25.52) * mm, "end": v(23.44, -25.52) * mm});
            skLineSegment(sketch, "E79.0.3", {"start": v(23.44, -25.52) * mm, "end": v(23.44, -25.02) * mm});
            skLineSegment(sketch, "E80.0.0", {"start": v(21.44, -25.02) * mm, "end": v(21.94, -25.02) * mm});
            skLineSegment(sketch, "E80.0.1", {"start": v(21.94, -25.02) * mm, "end": v(21.94, -25.52) * mm});
            skLineSegment(sketch, "E80.0.2", {"start": v(21.94, -25.52) * mm, "end": v(21.44, -25.52) * mm});
            skLineSegment(sketch, "E80.0.3", {"start": v(21.44, -25.52) * mm, "end": v(21.44, -25.02) * mm});
            skLineSegment(sketch, "E81.0.0", {"start": v(19.44, -25.02) * mm, "end": v(19.94, -25.02) * mm});
            skLineSegment(sketch, "E81.0.1", {"start": v(19.94, -25.02) * mm, "end": v(19.94, -25.52) * mm});
            skLineSegment(sketch, "E81.0.2", {"start": v(19.94, -25.52) * mm, "end": v(19.44, -25.52) * mm});
            skLineSegment(sketch, "E81.0.3", {"start": v(19.44, -25.52) * mm, "end": v(19.44, -25.02) * mm});
            skLineSegment(sketch, "E82.0.0", {"start": v(17.44, -25.02) * mm, "end": v(17.94, -25.02) * mm});
            skLineSegment(sketch, "E82.0.1", {"start": v(17.94, -25.02) * mm, "end": v(17.94, -25.52) * mm});
            skLineSegment(sketch, "E82.0.2", {"start": v(17.94, -25.52) * mm, "end": v(17.44, -25.52) * mm});
            skLineSegment(sketch, "E82.0.3", {"start": v(17.44, -25.52) * mm, "end": v(17.44, -25.02) * mm});
            skLineSegment(sketch, "E83.0.0", {"start": v(15.44, -25.02) * mm, "end": v(15.94, -25.02) * mm});
            skLineSegment(sketch, "E83.0.1", {"start": v(15.94, -25.02) * mm, "end": v(15.94, -25.52) * mm});
            skLineSegment(sketch, "E83.0.2", {"start": v(15.94, -25.52) * mm, "end": v(15.44, -25.52) * mm});
            skLineSegment(sketch, "E83.0.3", {"start": v(15.44, -25.52) * mm, "end": v(15.44, -25.02) * mm});
            skLineSegment(sketch, "E84.0.0", {"start": v(13.44, -25.02) * mm, "end": v(13.94, -25.02) * mm});
            skLineSegment(sketch, "E84.0.1", {"start": v(13.94, -25.02) * mm, "end": v(13.94, -25.52) * mm});
            skLineSegment(sketch, "E84.0.2", {"start": v(13.94, -25.52) * mm, "end": v(13.44, -25.52) * mm});
            skLineSegment(sketch, "E84.0.3", {"start": v(13.44, -25.52) * mm, "end": v(13.44, -25.02) * mm});
            skLineSegment(sketch, "E85.0.0", {"start": v(11.44, -25.02) * mm, "end": v(11.94, -25.02) * mm});
            skLineSegment(sketch, "E85.0.1", {"start": v(11.94, -25.02) * mm, "end": v(11.94, -25.52) * mm});
            skLineSegment(sketch, "E85.0.2", {"start": v(11.94, -25.52) * mm, "end": v(11.44, -25.52) * mm});
            skLineSegment(sketch, "E85.0.3", {"start": v(11.44, -25.52) * mm, "end": v(11.44, -25.02) * mm});
            skLineSegment(sketch, "E86.0.0", {"start": v(9.44, -25.02) * mm, "end": v(9.94, -25.02) * mm});
            skLineSegment(sketch, "E86.0.1", {"start": v(9.94, -25.02) * mm, "end": v(9.94, -25.52) * mm});
            skLineSegment(sketch, "E86.0.2", {"start": v(9.94, -25.52) * mm, "end": v(9.44, -25.52) * mm});
            skLineSegment(sketch, "E86.0.3", {"start": v(9.44, -25.52) * mm, "end": v(9.44, -25.02) * mm});
            skLineSegment(sketch, "E87.0.0", {"start": v(7.44, -25.02) * mm, "end": v(7.94, -25.02) * mm});
            skLineSegment(sketch, "E87.0.1", {"start": v(7.94, -25.02) * mm, "end": v(7.94, -25.52) * mm});
            skLineSegment(sketch, "E87.0.2", {"start": v(7.94, -25.52) * mm, "end": v(7.44, -25.52) * mm});
            skLineSegment(sketch, "E87.0.3", {"start": v(7.44, -25.52) * mm, "end": v(7.44, -25.02) * mm});
            skLineSegment(sketch, "E88.0.0", {"start": v(37.44, -0.74) * mm, "end": v(37.94, -0.74) * mm});
            skLineSegment(sketch, "E88.0.1", {"start": v(37.94, -0.74) * mm, "end": v(37.94, -1.24) * mm});
            skLineSegment(sketch, "E88.0.2", {"start": v(37.94, -1.24) * mm, "end": v(37.44, -1.24) * mm});
            skLineSegment(sketch, "E88.0.3", {"start": v(37.44, -1.24) * mm, "end": v(37.44, -0.74) * mm});
            skLineSegment(sketch, "E89.0.0", {"start": v(35.44, -0.74) * mm, "end": v(35.94, -0.74) * mm});
            skLineSegment(sketch, "E89.0.1", {"start": v(35.94, -0.74) * mm, "end": v(35.94, -1.24) * mm});
            skLineSegment(sketch, "E89.0.2", {"start": v(35.94, -1.24) * mm, "end": v(35.44, -1.24) * mm});
            skLineSegment(sketch, "E89.0.3", {"start": v(35.44, -1.24) * mm, "end": v(35.44, -0.74) * mm});
            skLineSegment(sketch, "E90.0.0", {"start": v(33.44, -0.74) * mm, "end": v(33.94, -0.74) * mm});
            skLineSegment(sketch, "E90.0.1", {"start": v(33.94, -0.74) * mm, "end": v(33.94, -1.24) * mm});
            skLineSegment(sketch, "E90.0.2", {"start": v(33.94, -1.24) * mm, "end": v(33.44, -1.24) * mm});
            skLineSegment(sketch, "E90.0.3", {"start": v(33.44, -1.24) * mm, "end": v(33.44, -0.74) * mm});
            skLineSegment(sketch, "E91.0.0", {"start": v(31.44, -0.74) * mm, "end": v(31.94, -0.74) * mm});
            skLineSegment(sketch, "E91.0.1", {"start": v(31.94, -0.74) * mm, "end": v(31.94, -1.24) * mm});
            skLineSegment(sketch, "E91.0.2", {"start": v(31.94, -1.24) * mm, "end": v(31.44, -1.24) * mm});
            skLineSegment(sketch, "E91.0.3", {"start": v(31.44, -1.24) * mm, "end": v(31.44, -0.74) * mm});
            skLineSegment(sketch, "E92.0.0", {"start": v(29.44, -0.74) * mm, "end": v(29.94, -0.74) * mm});
            skLineSegment(sketch, "E92.0.1", {"start": v(29.94, -0.74) * mm, "end": v(29.94, -1.24) * mm});
            skLineSegment(sketch, "E92.0.2", {"start": v(29.94, -1.24) * mm, "end": v(29.44, -1.24) * mm});
            skLineSegment(sketch, "E92.0.3", {"start": v(29.44, -1.24) * mm, "end": v(29.44, -0.74) * mm});
            skLineSegment(sketch, "E93.0.0", {"start": v(27.44, -0.74) * mm, "end": v(27.94, -0.74) * mm});
            skLineSegment(sketch, "E93.0.1", {"start": v(27.94, -0.74) * mm, "end": v(27.94, -1.24) * mm});
            skLineSegment(sketch, "E93.0.2", {"start": v(27.94, -1.24) * mm, "end": v(27.44, -1.24) * mm});
            skLineSegment(sketch, "E93.0.3", {"start": v(27.44, -1.24) * mm, "end": v(27.44, -0.74) * mm});
            skLineSegment(sketch, "E94.0.0", {"start": v(25.44, -0.74) * mm, "end": v(25.94, -0.74) * mm});
            skLineSegment(sketch, "E94.0.1", {"start": v(25.94, -0.74) * mm, "end": v(25.94, -1.24) * mm});
            skLineSegment(sketch, "E94.0.2", {"start": v(25.94, -1.24) * mm, "end": v(25.44, -1.24) * mm});
            skLineSegment(sketch, "E94.0.3", {"start": v(25.44, -1.24) * mm, "end": v(25.44, -0.74) * mm});
            skLineSegment(sketch, "E95.0.0", {"start": v(23.44, -0.74) * mm, "end": v(23.94, -0.74) * mm});
            skLineSegment(sketch, "E95.0.1", {"start": v(23.94, -0.74) * mm, "end": v(23.94, -1.24) * mm});
            skLineSegment(sketch, "E95.0.2", {"start": v(23.94, -1.24) * mm, "end": v(23.44, -1.24) * mm});
            skLineSegment(sketch, "E95.0.3", {"start": v(23.44, -1.24) * mm, "end": v(23.44, -0.74) * mm});
            skLineSegment(sketch, "E96.0.0", {"start": v(21.44, -0.74) * mm, "end": v(21.94, -0.74) * mm});
            skLineSegment(sketch, "E96.0.1", {"start": v(21.94, -0.74) * mm, "end": v(21.94, -1.24) * mm});
            skLineSegment(sketch, "E96.0.2", {"start": v(21.94, -1.24) * mm, "end": v(21.44, -1.24) * mm});
            skLineSegment(sketch, "E96.0.3", {"start": v(21.44, -1.24) * mm, "end": v(21.44, -0.74) * mm});
            skLineSegment(sketch, "E97.0.0", {"start": v(19.44, -0.74) * mm, "end": v(19.94, -0.74) * mm});
            skLineSegment(sketch, "E97.0.1", {"start": v(19.94, -0.74) * mm, "end": v(19.94, -1.24) * mm});
            skLineSegment(sketch, "E97.0.2", {"start": v(19.94, -1.24) * mm, "end": v(19.44, -1.24) * mm});
            skLineSegment(sketch, "E97.0.3", {"start": v(19.44, -1.24) * mm, "end": v(19.44, -0.74) * mm});
            skLineSegment(sketch, "E98.0.0", {"start": v(17.44, -0.74) * mm, "end": v(17.94, -0.74) * mm});
            skLineSegment(sketch, "E98.0.1", {"start": v(17.94, -0.74) * mm, "end": v(17.94, -1.24) * mm});
            skLineSegment(sketch, "E98.0.2", {"start": v(17.94, -1.24) * mm, "end": v(17.44, -1.24) * mm});
            skLineSegment(sketch, "E98.0.3", {"start": v(17.44, -1.24) * mm, "end": v(17.44, -0.74) * mm});
            skLineSegment(sketch, "E99.0.0", {"start": v(15.44, -0.74) * mm, "end": v(15.94, -0.74) * mm});
            skLineSegment(sketch, "E99.0.1", {"start": v(15.94, -0.74) * mm, "end": v(15.94, -1.24) * mm});
            skLineSegment(sketch, "E99.0.2", {"start": v(15.94, -1.24) * mm, "end": v(15.44, -1.24) * mm});
            skLineSegment(sketch, "E99.0.3", {"start": v(15.44, -1.24) * mm, "end": v(15.44, -0.74) * mm});
            skLineSegment(sketch, "E100.0.0", {"start": v(13.44, -0.74) * mm, "end": v(13.94, -0.74) * mm});
            skLineSegment(sketch, "E100.0.1", {"start": v(13.94, -0.74) * mm, "end": v(13.94, -1.24) * mm});
            skLineSegment(sketch, "E100.0.2", {"start": v(13.94, -1.24) * mm, "end": v(13.44, -1.24) * mm});
            skLineSegment(sketch, "E100.0.3", {"start": v(13.44, -1.24) * mm, "end": v(13.44, -0.74) * mm});
            skLineSegment(sketch, "E101.0.0", {"start": v(11.44, -0.74) * mm, "end": v(11.94, -0.74) * mm});
            skLineSegment(sketch, "E101.0.1", {"start": v(11.94, -0.74) * mm, "end": v(11.94, -1.24) * mm});
            skLineSegment(sketch, "E101.0.2", {"start": v(11.94, -1.24) * mm, "end": v(11.44, -1.24) * mm});
            skLineSegment(sketch, "E101.0.3", {"start": v(11.44, -1.24) * mm, "end": v(11.44, -0.74) * mm});
            skLineSegment(sketch, "E102.0.0", {"start": v(9.44, -0.74) * mm, "end": v(9.94, -0.74) * mm});
            skLineSegment(sketch, "E102.0.1", {"start": v(9.94, -0.74) * mm, "end": v(9.94, -1.24) * mm});
            skLineSegment(sketch, "E102.0.2", {"start": v(9.94, -1.24) * mm, "end": v(9.44, -1.24) * mm});
            skLineSegment(sketch, "E102.0.3", {"start": v(9.44, -1.24) * mm, "end": v(9.44, -0.74) * mm});
            skLineSegment(sketch, "E103.0.0", {"start": v(7.44, -0.74) * mm, "end": v(7.94, -0.74) * mm});
            skLineSegment(sketch, "E103.0.1", {"start": v(7.94, -0.74) * mm, "end": v(7.94, -1.24) * mm});
            skLineSegment(sketch, "E103.0.2", {"start": v(7.94, -1.24) * mm, "end": v(7.44, -1.24) * mm});
            skLineSegment(sketch, "E103.0.3", {"start": v(7.44, -1.24) * mm, "end": v(7.44, -0.74) * mm});
            skSolve(sketch);
        }
        {
            var Q0;
            Q0 = qSketchRegion(id + "F37", true);
            var Q1;
            Q1=qCreatedBy(id+"F34.planeOp",FACE);
            extrude(context, id + "F38", {"entities" : qUnion([Q0]), "operationType" : NewBodyOperationType.ADD, "endBound" : BoundingType.UP_TO_SURFACE, "endBoundEntityFace" : qUnion([Q1]), "depth" : 25 * mm});
        }
        {
            var Q0;
            Q0=makeQuery(id+"F9.opExtrude","SWEPT_FACE",FACE,{"disambiguationData":[OSD([sQuery(id+"F8.wireOp",EDGE,"E38")])]});
            var sketch = newSketch(context, id + "F39", { "sketchPlane" : qUnion([Q0])});
            skLineSegment(sketch, "E104.bottom", {"start": v(-17.97, 1.48) * mm, "end": v(-19.82, 1.48) * mm});
            skLineSegment(sketch, "E104.top", {"start": v(-17.97, 0.58) * mm, "end": v(-19.82, 0.58) * mm});
            skLineSegment(sketch, "E104.left", {"start": v(-17.97, 1.48) * mm, "end": v(-17.97, 0.58) * mm});
            skLineSegment(sketch, "E104.right", {"start": v(-19.82, 1.48) * mm, "end": v(-19.82, 0.58) * mm});
            skPoint(sketch, "E104.middle", {"position": v(-18.9, 1.03) * mm});
            skPoint(sketch, "E104.middle.positionSnap0", {"position": v(-18.9, 0) * mm});
            skPoint(sketch, "E104.centerSnap0", {"position": v(-18.9, 0) * mm});
            skLineSegment(sketch, "E105", {"start": v(-21.15, 2.05) * mm, "end": v(-16.65, 0) * mm, "construction": true});
            skSolve(sketch);
        }
        {
            var Q0;
            Q0 = qSketchRegion(id + "F39", true);
            extrude(context, id + "F40", {"entities" : qUnion([Q0]), "operationType" : NewBodyOperationType.ADD, "depth" : .7 * mm});
        }
        {
            var Q0;
            Q0=makeQuery(id+"F22.opExtrude","SWEPT_FACE",FACE,{"disambiguationData":[OSD([sQuery(id+"F11.wireOp",EDGE,"E48.right")])]});
            var sketch = newSketch(context, id + "F41", { "sketchPlane" : qUnion([Q0])});
            skLineSegment(sketch, "E106.bottom", {"start": v(7.3, 1.3) * mm, "end": v(6.06, 1.3) * mm});
            skLineSegment(sketch, "E106.top", {"start": v(7.3, 0.2) * mm, "end": v(6.06, 0.2) * mm});
            skLineSegment(sketch, "E106.left", {"start": v(7.3, 1.3) * mm, "end": v(7.3, 0.2) * mm});
            skLineSegment(sketch, "E106.right", {"start": v(6.06, 1.3) * mm, "end": v(6.06, 0.2) * mm});
            skPoint(sketch, "E106.middle", {"position": v(6.68, 0.75) * mm});
            skPoint(sketch, "E106.middle.positionSnap0", {"position": v(4.56, 0.75) * mm});
            skPoint(sketch, "E106.centerSnap0", {"position": v(4.56, 0.75) * mm});
            skSolve(sketch);
        }
        {
            var Q0;
            Q0=makeQuery(id+"F41.imprint","IMPRINT",FACE,{"disambiguationData":[TD([[makeQuery(id+"F41.imprint","IMPRINT",EDGE,{"derivedFrom":sQuery(id+"F41.wireOp",EDGE,"E106.bottom")}),1.0]])]});
            extrude(context, id + "F42", {"entities" : qUnion([Q0]), "operationType" : NewBodyOperationType.ADD, "depth" : 1.5 * mm});
        }
    });
